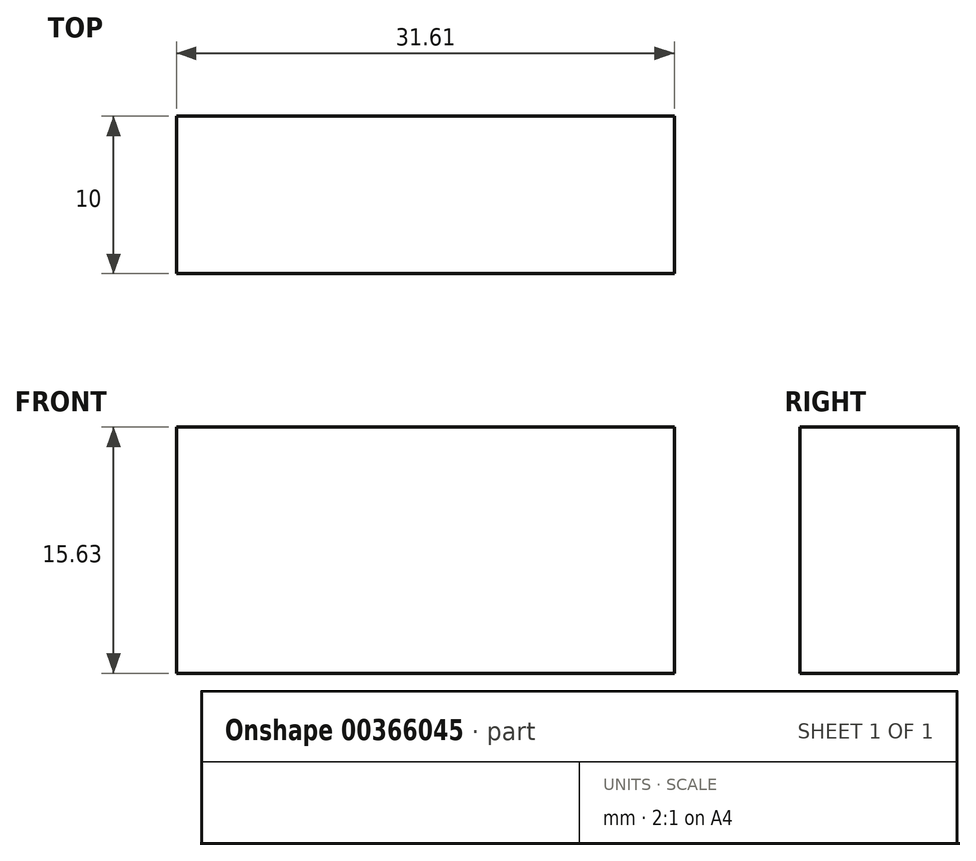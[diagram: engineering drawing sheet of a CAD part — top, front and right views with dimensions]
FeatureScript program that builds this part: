
annotation { "Feature Type Name" : "Feature", "Feature Type Description" : "" }
export const myFeature = defineFeature(function(context is Context, id is Id, definition is map)
    precondition{}
    {
        {
            var Q0;
            Q0=qCreatedBy(makeId("Front.planeOp"),FACE);
            var sketch = newSketch(context, id + "F0", { "sketchPlane" : qUnion([Q0])});
            skLineSegment(sketch, "E0.bottom", {"start": v(0, 0) * mm, "end": v(31.61, 0) * mm});
            skLineSegment(sketch, "E0.top", {"start": v(0, 15.63) * mm, "end": v(31.61, 15.63) * mm});
            skLineSegment(sketch, "E0.left", {"start": v(0, 0) * mm, "end": v(0, 15.63) * mm});
            skLineSegment(sketch, "E0.right", {"start": v(31.61, 0) * mm, "end": v(31.61, 15.63) * mm});
            skSolve(sketch);
        }
        {
            var Q0;
            Q0=makeQuery(id+"F0.imprint","IMPRINT",FACE,{"disambiguationData":[TD([[makeQuery(id+"F0.imprint","IMPRINT",EDGE,{"derivedFrom":sQuery(id+"F0.wireOp",EDGE,"E0.bottom")}),1.0]])]});
            extrude(context, id + "F1", {"entities" : qUnion([Q0]), "depth" : 10 * mm});
        }
    });
